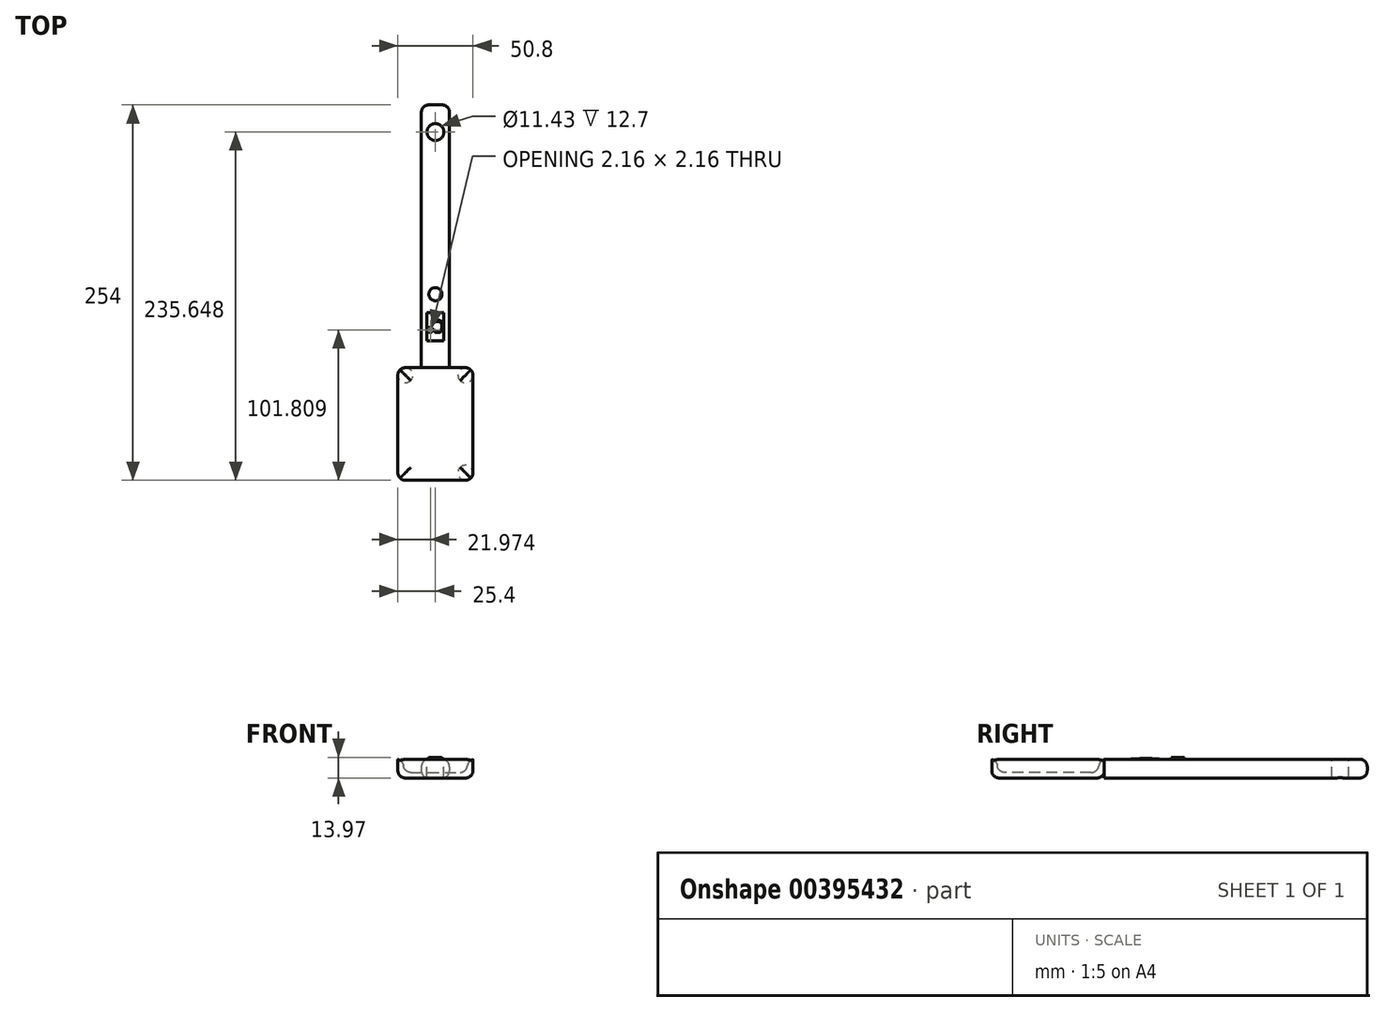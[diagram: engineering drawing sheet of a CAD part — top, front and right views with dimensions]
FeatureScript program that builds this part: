
annotation { "Feature Type Name" : "Feature", "Feature Type Description" : "" }
export const myFeature = defineFeature(function(context is Context, id is Id, definition is map)
    precondition{}
    {
        {
            var Q0;
            Q0=qCreatedBy(makeId("Front.planeOp"),FACE);
            var sketch = newSketch(context, id + "F0", { "sketchPlane" : qUnion([Q0])});
            skLineSegment(sketch, "E0.bottom", {"start": v(-9.53, 6.35) * mm, "end": v(9.53, 6.35) * mm});
            skLineSegment(sketch, "E0.top", {"start": v(-9.53, -6.35) * mm, "end": v(9.53, -6.35) * mm});
            skLineSegment(sketch, "E0.left", {"start": v(-9.53, 6.35) * mm, "end": v(-9.53, -6.35) * mm});
            skLineSegment(sketch, "E0.right", {"start": v(9.53, 6.35) * mm, "end": v(9.53, -6.35) * mm});
            skPoint(sketch, "E0.middle", {"position": v(0, 0) * mm});
            skSolve(sketch);
        }
        {
            var Q0;
            Q0 = qSketchRegion(id + "F0", true);
            extrude(context, id + "F1", {"entities" : qUnion([Q0]), "depth" : 177.8 * mm});
        }
        {
            var Q0;
            Q0=makeQuery(id+"F1.opExtrude","SWEPT_FACE",FACE,{"disambiguationData":[OSD([sQuery(id+"F0.wireOp",EDGE,"E0.bottom")])]});
            var sketch = newSketch(context, id + "F2", { "sketchPlane" : qUnion([Q0])});
            skCircle(sketch, "E1", {"center": v(0, -18.35) * mm, "radius": 5.72 * mm});
            skSolve(sketch);
        }
        {
            var Q0;
            Q0=sQuery(id+"F2.wireOp",VERTEX,"E1.center");
            var Q1;
            Q1=makeQuery(id+"F1.opExtrude","SWEPT_BODY",BODY,{"disambiguationData":[OSD([sQuery(id+"F0.wireOp",EDGE,"E0.bottom"),sQuery(id+"F0.wireOp",EDGE,"E0.top"),sQuery(id+"F0.wireOp",EDGE,"E0.left"),sQuery(id+"F0.wireOp",EDGE,"E0.right")])]});
            hole(context, id + "F3", {"style" : HoleStyle.SIMPLE, "endStyle" : HoleEndStyle.THROUGH, "holeDiameter" : 11.43 * mm, "isTappedThrough" : true, "tappedDepth" : 12.7 * mm, "tapClearance" : 3, "locations" : qUnion([Q0]), "scope" : qUnion([Q1])});
        }
        {
            var Q0;
            Q0=makeQuery(id+"F1.opExtrude","SWEPT_FACE",FACE,{"disambiguationData":[OSD([sQuery(id+"F0.wireOp",EDGE,"E0.bottom")])]});
            var sketch = newSketch(context, id + "F4", { "sketchPlane" : qUnion([Q0])});
            skLineSegment(sketch, "E2.bottom", {"start": v(-5.71, -140.67) * mm, "end": v(5.72, -140.67) * mm});
            skLineSegment(sketch, "E2.top", {"start": v(-5.72, -159.72) * mm, "end": v(5.71, -159.72) * mm});
            skLineSegment(sketch, "E2.left", {"start": v(-5.71, -140.67) * mm, "end": v(-5.72, -159.72) * mm});
            skLineSegment(sketch, "E2.right", {"start": v(5.72, -140.67) * mm, "end": v(5.71, -159.72) * mm});
            skPoint(sketch, "E2.middle", {"position": v(0, -150.2) * mm});
            skSolve(sketch);
        }
        {
            var Q0;
            Q0=makeQuery(id+"F4.imprint","IMPRINT",FACE,{"disambiguationData":[TD([[makeQuery(id+"F4.imprint","IMPRINT",EDGE,{"derivedFrom":sQuery(id+"F4.wireOp",EDGE,"E2.bottom")}),-1.0]])]});
            extrude(context, id + "F5", {"entities" : qUnion([Q0]), "depth" : 0.25 * mm});
        }
        {
            var Q0;
            Q0=makeQuery(id+"F1.opExtrude","SWEPT_FACE",FACE,{"disambiguationData":[OSD([sQuery(id+"F0.wireOp",EDGE,"E0.bottom")])]});
            var sketch = newSketch(context, id + "F6", { "sketchPlane" : qUnion([Q0])});
            skCircle(sketch, "E3", {"center": v(0, -128.12) * mm, "radius": 4.45 * mm});
            skSolve(sketch);
        }
        {
            var Q0;
            Q0=makeQuery(id+"F6.imprint","IMPRINT",FACE,{"disambiguationData":[TD([[makeQuery(id+"F6.imprint","IMPRINT",EDGE,{"derivedFrom":sQuery(id+"F6.wireOp",EDGE,"E3")}),1.0]])]});
            extrude(context, id + "F7", {"entities" : qUnion([Q0]), "depth" : 1.27 * mm});
        }
        {
            var Q0;
            Q0=makeQuery(id+"F5.opExtrude","CAP_FACE",FACE,{"disambiguationData":[OSD([sQuery(id+"F4.wireOp",EDGE,"E2.bottom"),sQuery(id+"F4.wireOp",EDGE,"E2.top"),sQuery(id+"F4.wireOp",EDGE,"E2.left"),sQuery(id+"F4.wireOp",EDGE,"E2.right")])],"isStart":false});
            var sketch = newSketch(context, id + "F8", { "sketchPlane" : qUnion([Q0])});
            skText(sketch, "E4", { "text": "C°", "fontName": "OpenSans-Regular.ttf"});
            const initialGuessF8  = {"E4": [0.00618, -0.14588, -0.9999, 0.01379, 0.00811]};
            skSetInitialGuess(sketch, initialGuessF8);
            skSolve(sketch);
        }
        {
            var Q0;
            Q0 = qSketchRegion(id + "F8", true);
            extrude(context, id + "F9", {"entities" : qUnion([Q0]), "depth" : 0.25 * mm});
        }
        {
            var Q0;
            Q0=makeQuery(id+"F1.opExtrude","SWEPT_FACE",FACE,{"disambiguationData":[OSD([sQuery(id+"F0.wireOp",EDGE,"E0.top")])]});
            var sketch = newSketch(context, id + "F10", { "sketchPlane" : qUnion([Q0])});
            skPoint(sketch, "E5", {"position": v(0, 215.9) * mm});
            skPoint(sketch, "E6", {"position": v(0, 177.8) * mm});
            skLineSegment(sketch, "E7.bottom", {"start": v(-25.4, 254) * mm, "end": v(25.4, 254) * mm});
            skLineSegment(sketch, "E7.top", {"start": v(-25.4, 177.8) * mm, "end": v(25.4, 177.8) * mm});
            skLineSegment(sketch, "E7.left", {"start": v(-25.4, 254) * mm, "end": v(-25.4, 177.8) * mm});
            skLineSegment(sketch, "E7.right", {"start": v(25.4, 254) * mm, "end": v(25.4, 177.8) * mm});
            skSolve(sketch);
        }
        {
            var Q0;
            Q0=makeQuery(id+"F10.imprint","IMPRINT",FACE,{"disambiguationData":[TD([[makeQuery(id+"F10.imprint","IMPRINT",EDGE,{"derivedFrom":sQuery(id+"F10.wireOp",EDGE,"E7.bottom")}),-1.0]])]});
            extrude(context, id + "F11", {"entities" : qUnion([Q0]), "oppositeDirection" : true, "depth" : 12.7 * mm});
        }
        {
            var Q0;
            Q0=makeQuery(id+"F11.opExtrude","CAP_FACE",FACE,{"disambiguationData":[OSD([sQuery(id+"F10.wireOp",EDGE,"E7.bottom"),sQuery(id+"F10.wireOp",EDGE,"E7.top"),sQuery(id+"F10.wireOp",EDGE,"E7.left"),sQuery(id+"F10.wireOp",EDGE,"E7.right")])],"isStart":false});
            shell(context, id + "F12", {"entities" : qUnion([Q0]), "thickness" : 3.8 * mm});
        }
        {
            var Q0;
            {var subQ0=sQuery(id+"F10.wireOp",EDGE,"E7.left");Q0=makeQuery(id+"F12.opShell","OFFSET_EDGE",EDGE,{"disambiguationData":[OSD([subQ0]),TDD([makeQuery(id+"F11.opExtrude","CAP_EDGE",EDGE,{"disambiguationData":[OSD([subQ0])],"isStart":false})])]});}
            var Q1;
            {var subQ0=sQuery(id+"F10.wireOp",EDGE,"E7.top");Q1=makeQuery(id+"F12.opShell","OFFSET_EDGE",EDGE,{"disambiguationData":[OSD([subQ0]),TDD([makeQuery(id+"F11.opExtrude","CAP_EDGE",EDGE,{"disambiguationData":[OSD([subQ0])],"isStart":false})])]});}
            var Q2;
            {var subQ0=sQuery(id+"F10.wireOp",EDGE,"E7.right");Q2=makeQuery(id+"F12.opShell","OFFSET_EDGE",EDGE,{"disambiguationData":[OSD([subQ0]),TDD([makeQuery(id+"F11.opExtrude","CAP_EDGE",EDGE,{"disambiguationData":[OSD([subQ0])],"isStart":false})])]});}
            var Q3;
            {var subQ0=sQuery(id+"F10.wireOp",EDGE,"E7.bottom");Q3=makeQuery(id+"F12.opShell","OFFSET_EDGE",EDGE,{"disambiguationData":[OSD([subQ0]),TDD([makeQuery(id+"F11.opExtrude","CAP_EDGE",EDGE,{"disambiguationData":[OSD([subQ0])],"isStart":false})])]});}
            fillet(context, id + "F13", {"entities" : qUnion([Q0, Q1, Q2, Q3]), "radius" : 5.08 * mm, "tangentPropagation" : true, "allowEdgeOverflow" : false});
        }
        {
            var Q0;
            Q0=makeQuery(id+"F12.opShell","OFFSET_FACE",FACE,{"disambiguationData":[OSD([sQuery(id+"F10.wireOp",EDGE,"E7.bottom"),sQuery(id+"F10.wireOp",EDGE,"E7.top"),sQuery(id+"F10.wireOp",EDGE,"E7.left"),sQuery(id+"F10.wireOp",EDGE,"E7.right")])]});
            fillet(context, id + "F14", {"entities" : qUnion([Q0]), "radius" : 5.08 * mm, "tangentPropagation" : true, "allowEdgeOverflow" : false});
        }
        {
            var Q0;
            Q0=makeQuery(id+"F11.opExtrude","SWEPT_EDGE",EDGE,{"disambiguationData":[OSD([sQuery(id+"F10.wireOp",EDGE,"E7.bottom"),sQuery(id+"F10.wireOp",EDGE,"E7.right")])]});
            var Q1;
            Q1=makeQuery(id+"F11.opExtrude","SWEPT_EDGE",EDGE,{"disambiguationData":[OSD([sQuery(id+"F10.wireOp",EDGE,"E7.bottom"),sQuery(id+"F10.wireOp",EDGE,"E7.left")])]});
            var Q2;
            Q2=makeQuery(id+"F11.opExtrude","CAP_FACE",FACE,{"disambiguationData":[OSD([sQuery(id+"F10.wireOp",EDGE,"E7.bottom"),sQuery(id+"F10.wireOp",EDGE,"E7.top"),sQuery(id+"F10.wireOp",EDGE,"E7.left"),sQuery(id+"F10.wireOp",EDGE,"E7.right")])],"isStart":true});
            var Q3;
            Q3=makeQuery(id+"F11.opExtrude","SWEPT_EDGE",EDGE,{"disambiguationData":[OSD([sQuery(id+"F10.wireOp",EDGE,"E7.top"),sQuery(id+"F10.wireOp",EDGE,"E7.right")])]});
            var Q4;
            Q4=makeQuery(id+"F11.opExtrude","SWEPT_EDGE",EDGE,{"disambiguationData":[OSD([sQuery(id+"F10.wireOp",EDGE,"E7.top"),sQuery(id+"F10.wireOp",EDGE,"E7.left")])]});
            var Q5;
            Q5=makeQuery(id+"F1.opExtrude","SWEPT_EDGE",EDGE,{"disambiguationData":[OSD([sQuery(id+"F0.wireOp",EDGE,"E0.bottom"),sQuery(id+"F0.wireOp",EDGE,"E0.right")])]});
            var Q6;
            Q6=makeQuery(id+"F1.opExtrude","SWEPT_EDGE",EDGE,{"disambiguationData":[OSD([sQuery(id+"F0.wireOp",EDGE,"E0.bottom"),sQuery(id+"F0.wireOp",EDGE,"E0.left")])]});
            var Q7;
            Q7=makeQuery(id+"F1.opExtrude","SWEPT_EDGE",EDGE,{"disambiguationData":[OSD([sQuery(id+"F0.wireOp",EDGE,"E0.top"),sQuery(id+"F0.wireOp",EDGE,"E0.right")])]});
            var Q8;
            Q8=makeQuery(id+"F1.opExtrude","SWEPT_EDGE",EDGE,{"disambiguationData":[OSD([sQuery(id+"F0.wireOp",EDGE,"E0.top"),sQuery(id+"F0.wireOp",EDGE,"E0.left")])]});
            var Q9;
            Q9=makeQuery(id+"F1.opExtrude","CAP_FACE",FACE,{"disambiguationData":[OSD([sQuery(id+"F0.wireOp",EDGE,"E0.bottom"),sQuery(id+"F0.wireOp",EDGE,"E0.top"),sQuery(id+"F0.wireOp",EDGE,"E0.left"),sQuery(id+"F0.wireOp",EDGE,"E0.right")])],"isStart":true});
            fillet(context, id + "F15", {"entities" : qUnion([Q0, Q1, Q2, Q3, Q4, Q5, Q6, Q7, Q8, Q9]), "radius" : 5.08 * mm, "tangentPropagation" : true, "allowEdgeOverflow" : false});
        }
    });
